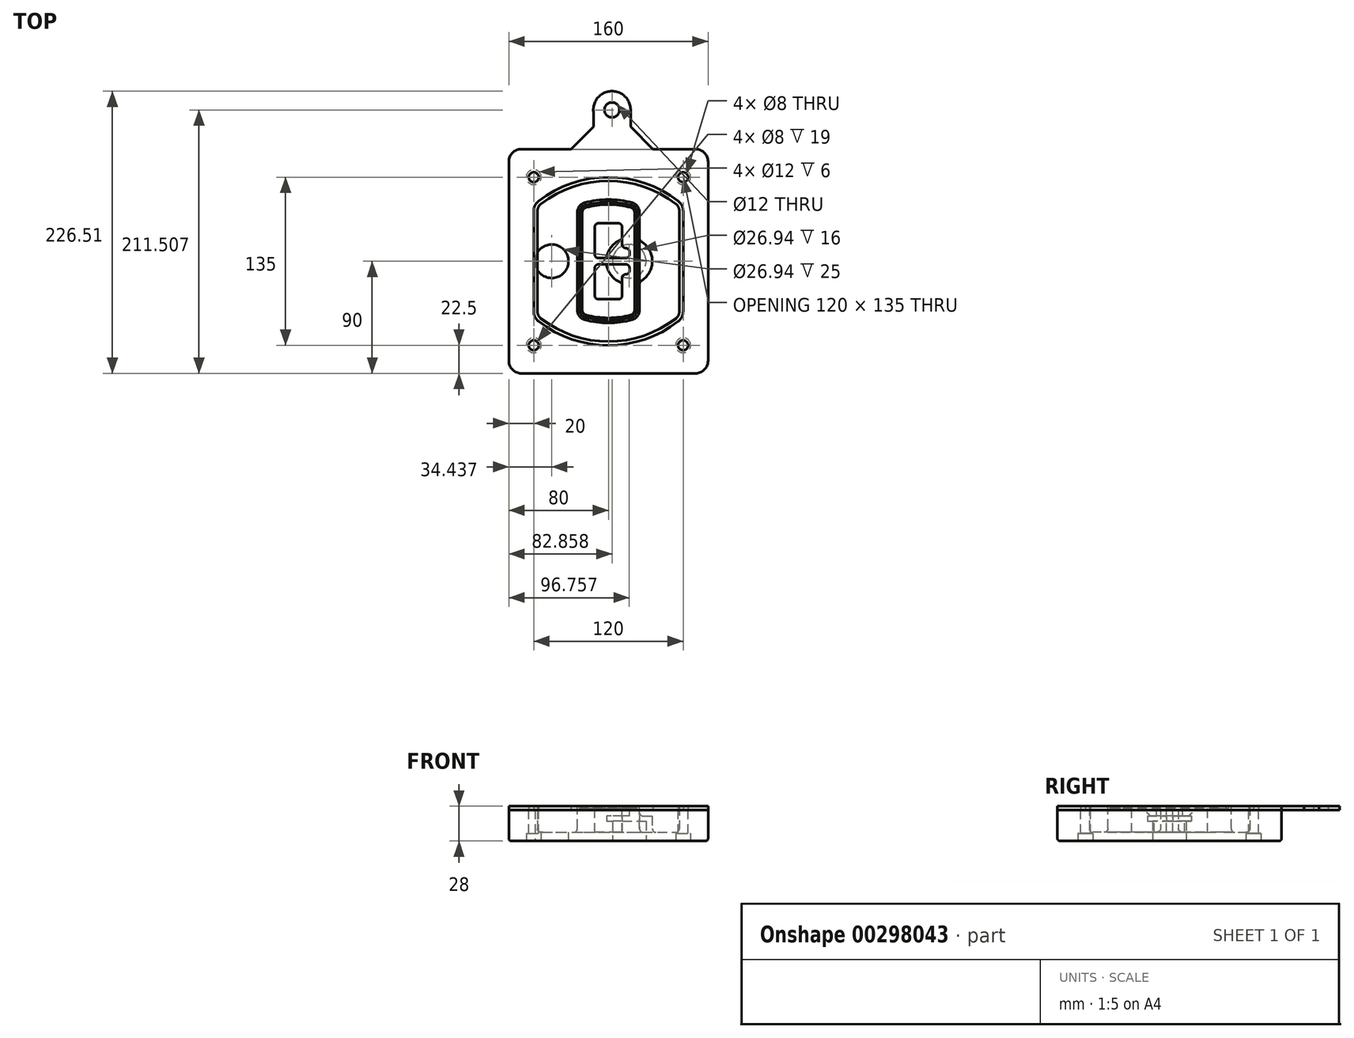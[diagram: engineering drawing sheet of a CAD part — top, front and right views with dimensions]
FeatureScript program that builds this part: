
annotation { "Feature Type Name" : "Feature", "Feature Type Description" : "" }
export const myFeature = defineFeature(function(context is Context, id is Id, definition is map)
    precondition{}
    {
        {
            var Q0;
            Q0=qCreatedBy(makeId("Top.planeOp"),FACE);
            var sketch = newSketch(context, id + "F0", { "sketchPlane" : qUnion([Q0])});
            skPoint(sketch, "E0.rect.middle", {"position": v(0, 0) * mm});
            skLineSegment(sketch, "E1.bottom", {"start": v(-70, -90) * mm, "end": v(70, -90) * mm});
            skLineSegment(sketch, "E1.top", {"start": v(-70, 90) * mm, "end": v(70, 90) * mm});
            skLineSegment(sketch, "E1.left", {"start": v(-80, -80) * mm, "end": v(-80, 80) * mm});
            skLineSegment(sketch, "E1.right", {"start": v(80, -80) * mm, "end": v(80, 80) * mm});
            skLineSegment(sketch, "E2", {"start": v(-80, 90) * mm, "end": v(80, -90) * mm, "construction": true});
            skLineSegment(sketch, "E3", {"start": v(80, 90) * mm, "end": v(-80, -90) * mm, "construction": true});
            skCircle(sketch, "E4", {"center": v(-60, 67.5) * mm, "radius": 4 * mm});
            skCircle(sketch, "E5", {"center": v(60, 67.5) * mm, "radius": 4 * mm});
            skCircle(sketch, "E6", {"center": v(60, -67.5) * mm, "radius": 4 * mm});
            skCircle(sketch, "E7", {"center": v(-60, -67.5) * mm, "radius": 4 * mm});
            skLineSegment(sketch, "E8", {"start": v(-60, 67.5) * mm, "end": v(60, 67.5) * mm, "construction": true});
            skLineSegment(sketch, "E9", {"start": v(60, 67.5) * mm, "end": v(60, -67.5) * mm, "construction": true});
            skLineSegment(sketch, "E10", {"start": v(60, -67.5) * mm, "end": v(-60, -67.5) * mm, "construction": true});
            skLineSegment(sketch, "E11", {"start": v(-60, -67.5) * mm, "end": v(-60, 67.5) * mm, "construction": true});
            skLineSegment(sketch, "E12", {"start": v(-60, 40.3) * mm, "end": v(-60, -40.3) * mm});
            skLineSegment(sketch, "E13", {"start": v(60, 40.3) * mm, "end": v(60, -40.3) * mm});
            skArc(sketch, "E14", {"start": v(56.15, 48.18) * mm, "mid": v(0, 67.5) * mm, "end": v(-56.15, 48.18) * mm});
            skArc(sketch, "E15", {"start": v(-56.15, -48.18) * mm, "mid": v(0, -67.5) * mm, "end": v(56.15, -48.18) * mm});
            skLineSegment(sketch, "E16", {"start": v(-60, 0) * mm, "end": v(60, 0) * mm, "construction": true});
            skPoint(sketch, "E17.visualSharp", {"position": v(-60, -45) * mm});
            skArc(sketch, "E17.filletArc", {"start": v(-60, -40.3) * mm, "mid": v(-58.99, -44.68) * mm, "end": v(-56.15, -48.18) * mm});
            skPoint(sketch, "E18.visualSharp", {"position": v(-60, 45) * mm});
            skArc(sketch, "E18.filletArc", {"start": v(-56.15, 48.18) * mm, "mid": v(-58.99, 44.68) * mm, "end": v(-60, 40.3) * mm});
            skPoint(sketch, "E19.visualSharp", {"position": v(60, 45) * mm});
            skArc(sketch, "E19.filletArc", {"start": v(60, 40.3) * mm, "mid": v(58.99, 44.68) * mm, "end": v(56.15, 48.18) * mm});
            skPoint(sketch, "E20.visualSharp", {"position": v(60, -45) * mm});
            skArc(sketch, "E20.filletArc", {"start": v(56.15, -48.18) * mm, "mid": v(58.99, -44.68) * mm, "end": v(60, -40.3) * mm});
            skPoint(sketch, "E21.visualSharp", {"position": v(-80, 90) * mm});
            skArc(sketch, "E21.filletArc", {"start": v(-70, 90) * mm, "mid": v(-77.07, 87.07) * mm, "end": v(-80, 80) * mm});
            skPoint(sketch, "E22.visualSharp", {"position": v(80, 90) * mm});
            skArc(sketch, "E22.filletArc", {"start": v(80, 80) * mm, "mid": v(77.07, 87.07) * mm, "end": v(70, 90) * mm});
            skPoint(sketch, "E23.visualSharp", {"position": v(80, -90) * mm});
            skArc(sketch, "E23.filletArc", {"start": v(70, -90) * mm, "mid": v(77.07, -87.07) * mm, "end": v(80, -80) * mm});
            skPoint(sketch, "E24.visualSharp", {"position": v(-80, -90) * mm});
            skArc(sketch, "E24.filletArc", {"start": v(-80, -80) * mm, "mid": v(-77.07, -87.07) * mm, "end": v(-70, -90) * mm});
            skArc(sketch, "E25.0", {"start": v(57, 40.3) * mm, "mid": v(56.3, 43.36) * mm, "end": v(54.3, 45.81) * mm});
            skLineSegment(sketch, "E25.1", {"start": v(57, 40.3) * mm, "end": v(57, -40.3) * mm});
            skArc(sketch, "E25.2", {"start": v(54.3, -45.81) * mm, "mid": v(56.3, -43.36) * mm, "end": v(57, -40.3) * mm});
            skArc(sketch, "E25.3", {"start": v(-54.3, -45.81) * mm, "mid": v(0, -64.5) * mm, "end": v(54.3, -45.81) * mm});
            skArc(sketch, "E25.4", {"start": v(-57, -40.3) * mm, "mid": v(-56.3, -43.36) * mm, "end": v(-54.3, -45.81) * mm});
            skArc(sketch, "E25.5", {"start": v(54.3, 45.81) * mm, "mid": v(0, 64.5) * mm, "end": v(-54.3, 45.81) * mm});
            skLineSegment(sketch, "E25.6", {"start": v(-57, 40.3) * mm, "end": v(-57, -40.3) * mm});
            skArc(sketch, "E25.7", {"start": v(-54.3, 45.81) * mm, "mid": v(-56.3, 43.36) * mm, "end": v(-57, 40.3) * mm});
            skArc(sketch, "E26.0", {"start": v(-58.62, 51.33) * mm, "mid": v(-62.58, 46.43) * mm, "end": v(-64, 40.3) * mm});
            skArc(sketch, "E26.1", {"start": v(58.62, 51.33) * mm, "mid": v(0, 71.5) * mm, "end": v(-58.62, 51.33) * mm});
            skArc(sketch, "E26.2", {"start": v(64, 40.3) * mm, "mid": v(62.58, 46.43) * mm, "end": v(58.62, 51.33) * mm});
            skLineSegment(sketch, "E26.3", {"start": v(64, 40.3) * mm, "end": v(64, -40.3) * mm});
            skArc(sketch, "E26.4", {"start": v(58.62, -51.33) * mm, "mid": v(62.58, -46.43) * mm, "end": v(64, -40.3) * mm});
            skLineSegment(sketch, "E26.5", {"start": v(-64, 40.3) * mm, "end": v(-64, -40.3) * mm});
            skArc(sketch, "E26.6", {"start": v(-58.62, -51.33) * mm, "mid": v(0, -71.5) * mm, "end": v(58.62, -51.33) * mm});
            skArc(sketch, "E26.7", {"start": v(-64, -40.3) * mm, "mid": v(-62.58, -46.43) * mm, "end": v(-58.62, -51.33) * mm});
            skSolve(sketch);
        }
        {
            var Q0;
            Q0=makeQuery(id+"F0.imprint","IMPRINT",FACE,{"disambiguationData":[TD([[makeQuery(id+"F0.imprint","IMPRINT",EDGE,{"derivedFrom":sQuery(id+"F0.wireOp",EDGE,"E1.bottom")}),1.0]])]});
            var Q1;
            Q1=makeQuery(id+"F0.imprint","IMPRINT",FACE,{"disambiguationData":[TD([[makeQuery(id+"F0.imprint","IMPRINT",EDGE,{"derivedFrom":sQuery(id+"F0.wireOp",EDGE,"E12")}),1.0]])]});
            var Q2;
            Q2=makeQuery(id+"F0.imprint","IMPRINT",FACE,{"disambiguationData":[TD([[makeQuery(id+"F0.imprint","IMPRINT",EDGE,{"derivedFrom":sQuery(id+"F0.wireOp",EDGE,"E25.0")}),1.0]])]});
            var Q3;
            Q3=makeQuery(id+"F0.imprint","IMPRINT",FACE,{"disambiguationData":[TD([[makeQuery(id+"F0.imprint","IMPRINT",EDGE,{"derivedFrom":sQuery(id+"F0.wireOp",EDGE,"E12")}),-1.0]])]});
            extrude(context, id + "F1", {"entities" : qUnion([Q0, Q1, Q2, Q3]), "oppositeDirection" : true, "depth" : 25 * mm});
        }
        {
            var Q0;
            Q0=makeQuery(id+"F0.imprint","IMPRINT",FACE,{"disambiguationData":[TD([[makeQuery(id+"F0.imprint","IMPRINT",EDGE,{"derivedFrom":sQuery(id+"F0.wireOp",EDGE,"E12")}),1.0]])]});
            extrude(context, id + "F2", {"entities" : qUnion([Q0]), "operationType" : NewBodyOperationType.ADD, "depth" : 3 * mm});
        }
        {
            var Q0;
            Q0=makeQuery(id+"F0.imprint","IMPRINT",FACE,{"disambiguationData":[TD([[makeQuery(id+"F0.imprint","IMPRINT",EDGE,{"derivedFrom":sQuery(id+"F0.wireOp",EDGE,"E25.0")}),1.0]])]});
            extrude(context, id + "F3", {"entities" : qUnion([Q0]), "operationType" : NewBodyOperationType.REMOVE, "oppositeDirection" : true, "depth" : 18 * mm});
        }
        {
            var Q0;
            Q0=makeQuery(id+"F2.opExtrude","CAP_FACE",FACE,{"disambiguationData":[OSD([sQuery(id+"F0.wireOp",EDGE,"E12"),sQuery(id+"F0.wireOp",EDGE,"E13"),sQuery(id+"F0.wireOp",EDGE,"E14"),sQuery(id+"F0.wireOp",EDGE,"E15"),sQuery(id+"F0.wireOp",EDGE,"E17.filletArc"),sQuery(id+"F0.wireOp",EDGE,"E18.filletArc"),sQuery(id+"F0.wireOp",EDGE,"E19.filletArc"),sQuery(id+"F0.wireOp",EDGE,"E20.filletArc"),sQuery(id+"F0.wireOp",EDGE,"E25.0"),sQuery(id+"F0.wireOp",EDGE,"E25.1"),sQuery(id+"F0.wireOp",EDGE,"E25.2"),sQuery(id+"F0.wireOp",EDGE,"E25.3"),sQuery(id+"F0.wireOp",EDGE,"E25.4"),sQuery(id+"F0.wireOp",EDGE,"E25.5"),sQuery(id+"F0.wireOp",EDGE,"E25.6"),sQuery(id+"F0.wireOp",EDGE,"E25.7")])],"isStart":false});
            var sketch = newSketch(context, id + "F4", { "sketchPlane" : qUnion([Q0])});
            skArc(sketch, "E27.0", {"start": v(-19.08, -46.97) * mm, "mid": v(0, -49.5) * mm, "end": v(19.08, -46.97) * mm});
            skArc(sketch, "E28.0", {"start": v(19.08, 46.97) * mm, "mid": v(0, 49.5) * mm, "end": v(-19.08, 46.97) * mm});
            skLineSegment(sketch, "E29", {"start": v(-25, 39.25) * mm, "end": v(-25, -39.25) * mm});
            skLineSegment(sketch, "E30", {"start": v(25, 39.25) * mm, "end": v(25, -39.25) * mm});
            skLineSegment(sketch, "E31", {"start": v(-25, 45.1) * mm, "end": v(25, 45.1) * mm, "construction": true});
            skLineSegment(sketch, "E32", {"start": v(-25, -45.1) * mm, "end": v(25, -45.1) * mm, "construction": true});
            skPoint(sketch, "E33.visualSharp", {"position": v(-25, 45.1) * mm});
            skArc(sketch, "E33.filletArc", {"start": v(-19.08, 46.97) * mm, "mid": v(-23.35, 44.11) * mm, "end": v(-25, 39.25) * mm});
            skPoint(sketch, "E34.visualSharp", {"position": v(25, 45.1) * mm});
            skArc(sketch, "E34.filletArc", {"start": v(25, 39.25) * mm, "mid": v(23.35, 44.11) * mm, "end": v(19.08, 46.97) * mm});
            skPoint(sketch, "E35.visualSharp", {"position": v(25, -45.1) * mm});
            skArc(sketch, "E35.filletArc", {"start": v(19.08, -46.97) * mm, "mid": v(23.35, -44.11) * mm, "end": v(25, -39.25) * mm});
            skPoint(sketch, "E36.visualSharp", {"position": v(-25, -45.1) * mm});
            skArc(sketch, "E36.filletArc", {"start": v(-25, -39.25) * mm, "mid": v(-23.35, -44.11) * mm, "end": v(-19.08, -46.97) * mm});
            skArc(sketch, "E37.0", {"start": v(54.3, 45.81) * mm, "mid": v(0, 64.5) * mm, "end": v(-54.3, 45.81) * mm});
            skArc(sketch, "E37.1", {"start": v(-54.3, 45.81) * mm, "mid": v(-56.3, 43.36) * mm, "end": v(-57, 40.3) * mm});
            skLineSegment(sketch, "E37.2", {"start": v(-57, 40.3) * mm, "end": v(-57, -40.3) * mm});
            skArc(sketch, "E37.3", {"start": v(-57, -40.3) * mm, "mid": v(-56.3, -43.36) * mm, "end": v(-54.3, -45.81) * mm});
            skArc(sketch, "E37.4", {"start": v(-54.3, -45.81) * mm, "mid": v(0, -64.5) * mm, "end": v(54.3, -45.81) * mm});
            skArc(sketch, "E37.5", {"start": v(54.3, -45.81) * mm, "mid": v(56.3, -43.36) * mm, "end": v(57, -40.3) * mm});
            skLineSegment(sketch, "E37.6", {"start": v(57, 40.3) * mm, "end": v(57, -40.3) * mm});
            skArc(sketch, "E37.7", {"start": v(57, 40.3) * mm, "mid": v(56.3, 43.36) * mm, "end": v(54.3, 45.81) * mm});
            skLineSegment(sketch, "E38.0", {"start": v(23, 39.25) * mm, "end": v(23, -39.25) * mm});
            skArc(sketch, "E38.1", {"start": v(18.56, -45.04) * mm, "mid": v(21.76, -42.9) * mm, "end": v(23, -39.25) * mm});
            skArc(sketch, "E38.2", {"start": v(-18.56, -45.04) * mm, "mid": v(0, -47.5) * mm, "end": v(18.56, -45.04) * mm});
            skArc(sketch, "E38.3", {"start": v(-23, -39.25) * mm, "mid": v(-21.76, -42.9) * mm, "end": v(-18.56, -45.04) * mm});
            skLineSegment(sketch, "E38.4", {"start": v(-23, 39.25) * mm, "end": v(-23, -39.25) * mm});
            skArc(sketch, "E38.5", {"start": v(23, 39.25) * mm, "mid": v(21.76, 42.9) * mm, "end": v(18.56, 45.04) * mm});
            skArc(sketch, "E38.6", {"start": v(-18.56, 45.04) * mm, "mid": v(-21.76, 42.9) * mm, "end": v(-23, 39.25) * mm});
            skArc(sketch, "E38.7", {"start": v(18.56, 45.04) * mm, "mid": v(0, 47.5) * mm, "end": v(-18.56, 45.04) * mm});
            skArc(sketch, "E39.0", {"start": v(21, 39.25) * mm, "mid": v(20.18, 41.68) * mm, "end": v(18.04, 43.1) * mm});
            skLineSegment(sketch, "E39.1", {"start": v(21, 39.25) * mm, "end": v(21, -39.25) * mm});
            skArc(sketch, "E39.2", {"start": v(18.04, -43.1) * mm, "mid": v(20.18, -41.68) * mm, "end": v(21, -39.25) * mm});
            skArc(sketch, "E39.3", {"start": v(-18.04, -43.1) * mm, "mid": v(0, -45.5) * mm, "end": v(18.04, -43.1) * mm});
            skArc(sketch, "E39.4", {"start": v(-21, -39.25) * mm, "mid": v(-20.18, -41.68) * mm, "end": v(-18.04, -43.1) * mm});
            skArc(sketch, "E39.5", {"start": v(18.04, 43.1) * mm, "mid": v(0, 45.5) * mm, "end": v(-18.04, 43.1) * mm});
            skLineSegment(sketch, "E39.6", {"start": v(-21, 39.25) * mm, "end": v(-21, -39.25) * mm});
            skArc(sketch, "E39.7", {"start": v(-18.04, 43.1) * mm, "mid": v(-20.18, 41.68) * mm, "end": v(-21, 39.25) * mm});
            skLineSegment(sketch, "E40", {"start": v(-25, 0) * mm, "end": v(25, 0) * mm, "construction": true});
            skLineSegment(sketch, "E41", {"start": v(-11, 5.5) * mm, "end": v(-11, 27.5) * mm});
            skLineSegment(sketch, "E42", {"start": v(-8, 30.5) * mm, "end": v(8, 30.5) * mm});
            skLineSegment(sketch, "E43", {"start": v(11, 27.5) * mm, "end": v(11, 13.5) * mm});
            skLineSegment(sketch, "E44", {"start": v(14, 10.5) * mm, "end": v(14, 10.5) * mm});
            skLineSegment(sketch, "E45", {"start": v(17, 7.5) * mm, "end": v(17, 5.5) * mm});
            skLineSegment(sketch, "E46", {"start": v(14, 2.5) * mm, "end": v(-8, 2.5) * mm});
            skPoint(sketch, "E47.visualSharp", {"position": v(-11, 30.5) * mm});
            skArc(sketch, "E47.filletArc", {"start": v(-8, 30.5) * mm, "mid": v(-10.12, 29.62) * mm, "end": v(-11, 27.5) * mm});
            skPoint(sketch, "E48.visualSharp", {"position": v(11, 30.5) * mm});
            skArc(sketch, "E48.filletArc", {"start": v(11, 27.5) * mm, "mid": v(10.12, 29.62) * mm, "end": v(8, 30.5) * mm});
            skPoint(sketch, "E49.visualSharp", {"position": v(11, 10.5) * mm});
            skArc(sketch, "E49.filletArc", {"start": v(11, 13.5) * mm, "mid": v(11.88, 11.38) * mm, "end": v(14, 10.5) * mm});
            skPoint(sketch, "E50.visualSharp", {"position": v(17, 10.5) * mm});
            skArc(sketch, "E50.filletArc", {"start": v(17, 7.5) * mm, "mid": v(16.12, 9.62) * mm, "end": v(14, 10.5) * mm});
            skPoint(sketch, "E51.visualSharp", {"position": v(17, 2.5) * mm});
            skArc(sketch, "E51.filletArc", {"start": v(14, 2.5) * mm, "mid": v(16.12, 3.38) * mm, "end": v(17, 5.5) * mm});
            skPoint(sketch, "E52.visualSharp", {"position": v(-11, 2.5) * mm});
            skArc(sketch, "E52.filletArc", {"start": v(-11, 5.5) * mm, "mid": v(-10.12, 3.38) * mm, "end": v(-8, 2.5) * mm});
            skLineSegment(sketch, "E53.0.MirrorCS", {"start": v(14, -2.5) * mm, "end": v(-8, -2.5) * mm});
            skArc(sketch, "E54.0.MirrorCS", {"start": v(-11, -5.5) * mm, "mid": v(-10.12, -3.38) * mm, "end": v(-8, -2.5) * mm});
            skLineSegment(sketch, "E55.0.MirrorCS", {"start": v(-11, -5.5) * mm, "end": v(-11, -27.5) * mm});
            skArc(sketch, "E56.0.MirrorCS", {"start": v(-8, -30.5) * mm, "mid": v(-10.12, -29.62) * mm, "end": v(-11, -27.5) * mm});
            skLineSegment(sketch, "E57.0.MirrorCS", {"start": v(-8, -30.5) * mm, "end": v(8, -30.5) * mm});
            skArc(sketch, "E58.0.MirrorCS", {"start": v(11, -27.5) * mm, "mid": v(10.12, -29.62) * mm, "end": v(8, -30.5) * mm});
            skLineSegment(sketch, "E59.0.MirrorCS", {"start": v(11, -27.5) * mm, "end": v(11, -13.5) * mm});
            skArc(sketch, "E60.0.MirrorCS", {"start": v(11, -13.5) * mm, "mid": v(11.88, -11.38) * mm, "end": v(14, -10.5) * mm});
            skArc(sketch, "E61.0.MirrorCS", {"start": v(17, -7.5) * mm, "mid": v(16.12, -9.62) * mm, "end": v(14, -10.5) * mm});
            skLineSegment(sketch, "E62.0.MirrorCS", {"start": v(17, -7.5) * mm, "end": v(17, -5.5) * mm});
            skArc(sketch, "E63.0.MirrorCS", {"start": v(14, -2.5) * mm, "mid": v(16.12, -3.38) * mm, "end": v(17, -5.5) * mm});
            skSolve(sketch);
        }
        {
            var Q0;
            Q0=makeQuery(id+"F4.imprint","IMPRINT",FACE,{"disambiguationData":[TD([[makeQuery(id+"F4.imprint","IMPRINT",EDGE,{"derivedFrom":sQuery(id+"F4.wireOp",EDGE,"E27.0")}),1.0]])]});
            var Q1;
            Q1=makeQuery(id+"F4.imprint","IMPRINT",FACE,{"disambiguationData":[TD([[makeQuery(id+"F4.imprint","IMPRINT",EDGE,{"derivedFrom":sQuery(id+"F4.wireOp",EDGE,"E38.0")}),-1.0]])]});
            var Q2;
            Q2=makeQuery(id+"F4.imprint","IMPRINT",FACE,{"disambiguationData":[TD([[makeQuery(id+"F4.imprint","IMPRINT",EDGE,{"derivedFrom":sQuery(id+"F4.wireOp",EDGE,"E39.0")}),1.0]])]});
            extrude(context, id + "F5", {"entities" : qUnion([Q0, Q1, Q2]), "operationType" : NewBodyOperationType.ADD, "endBound" : BoundingType.UP_TO_NEXT, "oppositeDirection" : true, "depth" : 25 * mm});
        }
        {
            var Q0;
            Q0=makeQuery(id+"F4.imprint","IMPRINT",FACE,{"disambiguationData":[TD([[makeQuery(id+"F4.imprint","IMPRINT",EDGE,{"derivedFrom":sQuery(id+"F4.wireOp",EDGE,"E38.0")}),-1.0]])]});
            extrude(context, id + "F6", {"entities" : qUnion([Q0]), "operationType" : NewBodyOperationType.REMOVE, "oppositeDirection" : true, "depth" : 2 * mm});
        }
        {
            var Q0;
            Q0=makeQuery(id+"F1.opExtrude","CAP_FACE",FACE,{"disambiguationData":[OSD([sQuery(id+"F0.wireOp",EDGE,"E1.bottom"),sQuery(id+"F0.wireOp",EDGE,"E1.top"),sQuery(id+"F0.wireOp",EDGE,"E1.left"),sQuery(id+"F0.wireOp",EDGE,"E1.right"),sQuery(id+"F0.wireOp",EDGE,"E4"),sQuery(id+"F0.wireOp",EDGE,"E5"),sQuery(id+"F0.wireOp",EDGE,"E6"),sQuery(id+"F0.wireOp",EDGE,"E7"),sQuery(id+"F0.wireOp",EDGE,"E21.filletArc"),sQuery(id+"F0.wireOp",EDGE,"E22.filletArc"),sQuery(id+"F0.wireOp",EDGE,"E23.filletArc"),sQuery(id+"F0.wireOp",EDGE,"E24.filletArc")])],"isStart":false});
            var sketch = newSketch(context, id + "F7", { "sketchPlane" : qUnion([Q0])});
            skCircle(sketch, "E64", {"center": v(16.76, 0) * mm, "radius": 13.47 * mm});
            skCircle(sketch, "E65", {"center": v(-45.56, 0) * mm, "radius": 13.47 * mm});
            skLineSegment(sketch, "E66", {"start": v(80, 0) * mm, "end": v(-80, 0) * mm});
            skCircle(sketch, "E67", {"center": v(16.76, 0) * mm, "radius": 18.47 * mm});
            skCircle(sketch, "E68", {"center": v(60, -67.5) * mm, "radius": 6 * mm});
            skCircle(sketch, "E69", {"center": v(-60, -67.5) * mm, "radius": 6 * mm});
            skCircle(sketch, "E70", {"center": v(-60, 67.5) * mm, "radius": 6 * mm});
            skCircle(sketch, "E71", {"center": v(60, 67.5) * mm, "radius": 6 * mm});
            skSolve(sketch);
        }
        {
            var Q0;
            {var subQ1=sQuery(id+"F7.wireOp",EDGE,"E66");var subQ4=sQuery(id+"F7.wireOp",EDGE,"E64");var subQ6=makeQuery(id+"F7.imprint","INTERSECT",VERTEX,{"disambiguationData":[OD(0.0)],"derivedFrom":[subQ4,subQ1]});Q0=makeQuery(id+"F7.imprint","IMPRINT",FACE,{"disambiguationData":[TD([[makeQuery(id+"F7.imprint","IMPRINT",EDGE,{"disambiguationData":[TD([[subQ6,-1.0]])],"derivedFrom":subQ4}),-1.0]])]});}
            var Q1;
            {var subQ0=sQuery(id+"F7.wireOp",EDGE,"E66");var subQ1=sQuery(id+"F7.wireOp",EDGE,"E64");var subQ3=makeQuery(id+"F7.imprint","INTERSECT",VERTEX,{"disambiguationData":[OD(0.0)],"derivedFrom":[subQ1,subQ0]});Q1=makeQuery(id+"F7.imprint","IMPRINT",FACE,{"disambiguationData":[TD([[makeQuery(id+"F7.imprint","IMPRINT",EDGE,{"disambiguationData":[TD([[subQ3,-1.0]])],"derivedFrom":subQ1}),1.0]])]});}
            var Q2;
            {var subQ0=sQuery(id+"F7.wireOp",EDGE,"E66");var subQ1=sQuery(id+"F7.wireOp",EDGE,"E64");var subQ3=makeQuery(id+"F7.imprint","INTERSECT",VERTEX,{"disambiguationData":[OD(0.0)],"derivedFrom":[subQ1,subQ0]});Q2=makeQuery(id+"F7.imprint","IMPRINT",FACE,{"disambiguationData":[TD([[makeQuery(id+"F7.imprint","IMPRINT",EDGE,{"disambiguationData":[TD([[subQ3,1.0]])],"derivedFrom":subQ1}),1.0]])]});}
            var Q3;
            {var subQ1=sQuery(id+"F7.wireOp",EDGE,"E66");var subQ4=sQuery(id+"F7.wireOp",EDGE,"E64");var subQ6=makeQuery(id+"F7.imprint","INTERSECT",VERTEX,{"disambiguationData":[OD(0.0)],"derivedFrom":[subQ4,subQ1]});Q3=makeQuery(id+"F7.imprint","IMPRINT",FACE,{"disambiguationData":[TD([[makeQuery(id+"F7.imprint","IMPRINT",EDGE,{"disambiguationData":[TD([[subQ6,1.0]])],"derivedFrom":subQ4}),-1.0]])]});}
            extrude(context, id + "F8", {"entities" : qUnion([Q0, Q1, Q2, Q3]), "operationType" : NewBodyOperationType.ADD, "oppositeDirection" : true, "depth" : 20 * mm});
        }
        {
            var Q0;
            {var subQ0=sQuery(id+"F7.wireOp",EDGE,"E66");var subQ1=sQuery(id+"F7.wireOp",EDGE,"E64");var subQ3=makeQuery(id+"F7.imprint","INTERSECT",VERTEX,{"disambiguationData":[OD(0.0)],"derivedFrom":[subQ1,subQ0]});Q0=makeQuery(id+"F7.imprint","IMPRINT",FACE,{"disambiguationData":[TD([[makeQuery(id+"F7.imprint","IMPRINT",EDGE,{"disambiguationData":[TD([[subQ3,-1.0]])],"derivedFrom":subQ1}),1.0]])]});}
            var Q1;
            {var subQ0=sQuery(id+"F7.wireOp",EDGE,"E66");var subQ1=sQuery(id+"F7.wireOp",EDGE,"E64");var subQ3=makeQuery(id+"F7.imprint","INTERSECT",VERTEX,{"disambiguationData":[OD(0.0)],"derivedFrom":[subQ1,subQ0]});Q1=makeQuery(id+"F7.imprint","IMPRINT",FACE,{"disambiguationData":[TD([[makeQuery(id+"F7.imprint","IMPRINT",EDGE,{"disambiguationData":[TD([[subQ3,1.0]])],"derivedFrom":subQ1}),1.0]])]});}
            extrude(context, id + "F9", {"entities" : qUnion([Q0, Q1]), "operationType" : NewBodyOperationType.REMOVE, "oppositeDirection" : true, "depth" : 16 * mm});
        }
        {
            var Q0;
            {var subQ0=sQuery(id+"F7.wireOp",EDGE,"E66");var subQ1=sQuery(id+"F7.wireOp",EDGE,"E65");var subQ3=makeQuery(id+"F7.imprint","INTERSECT",VERTEX,{"disambiguationData":[OD(0.0)],"derivedFrom":[subQ1,subQ0]});Q0=makeQuery(id+"F7.imprint","IMPRINT",FACE,{"disambiguationData":[TD([[makeQuery(id+"F7.imprint","IMPRINT",EDGE,{"disambiguationData":[TD([[subQ3,-1.0]])],"derivedFrom":subQ1}),1.0]])]});}
            var Q1;
            {var subQ0=sQuery(id+"F7.wireOp",EDGE,"E66");var subQ1=sQuery(id+"F7.wireOp",EDGE,"E65");var subQ3=makeQuery(id+"F7.imprint","INTERSECT",VERTEX,{"disambiguationData":[OD(0.0)],"derivedFrom":[subQ1,subQ0]});Q1=makeQuery(id+"F7.imprint","IMPRINT",FACE,{"disambiguationData":[TD([[makeQuery(id+"F7.imprint","IMPRINT",EDGE,{"disambiguationData":[TD([[subQ3,1.0]])],"derivedFrom":subQ1}),1.0]])]});}
            extrude(context, id + "F10", {"entities" : qUnion([Q0, Q1]), "operationType" : NewBodyOperationType.REMOVE, "oppositeDirection" : true, "depth" : 25 * mm});
        }
        {
            var Q0;
            Q0=makeQuery(id+"F7.imprint","IMPRINT",FACE,{"disambiguationData":[TD([[makeQuery(id+"F7.imprint","IMPRINT",EDGE,{"derivedFrom":sQuery(id+"F7.wireOp",EDGE,"E68")}),1.0]])]});
            var Q1;
            Q1=makeQuery(id+"F7.imprint","IMPRINT",FACE,{"disambiguationData":[TD([[makeQuery(id+"F7.imprint","IMPRINT",EDGE,{"derivedFrom":makeQuery(id+"F1.opExtrude","CAP_EDGE",EDGE,{"disambiguationData":[OSD([sQuery(id+"F0.wireOp",EDGE,"E5")])],"isStart":false})}),-1.0]])]});
            var Q2;
            Q2=makeQuery(id+"F7.imprint","IMPRINT",FACE,{"disambiguationData":[TD([[makeQuery(id+"F7.imprint","IMPRINT",EDGE,{"derivedFrom":sQuery(id+"F7.wireOp",EDGE,"E69")}),1.0]])]});
            var Q3;
            Q3=makeQuery(id+"F7.imprint","IMPRINT",FACE,{"disambiguationData":[TD([[makeQuery(id+"F7.imprint","IMPRINT",EDGE,{"derivedFrom":makeQuery(id+"F1.opExtrude","CAP_EDGE",EDGE,{"disambiguationData":[OSD([sQuery(id+"F0.wireOp",EDGE,"E4")])],"isStart":false})}),-1.0]])]});
            var Q4;
            Q4=makeQuery(id+"F7.imprint","IMPRINT",FACE,{"disambiguationData":[TD([[makeQuery(id+"F7.imprint","IMPRINT",EDGE,{"derivedFrom":sQuery(id+"F7.wireOp",EDGE,"E70")}),1.0]])]});
            var Q5;
            Q5=makeQuery(id+"F7.imprint","IMPRINT",FACE,{"disambiguationData":[TD([[makeQuery(id+"F7.imprint","IMPRINT",EDGE,{"derivedFrom":makeQuery(id+"F1.opExtrude","CAP_EDGE",EDGE,{"disambiguationData":[OSD([sQuery(id+"F0.wireOp",EDGE,"E7")])],"isStart":false})}),-1.0]])]});
            var Q6;
            Q6=makeQuery(id+"F7.imprint","IMPRINT",FACE,{"disambiguationData":[TD([[makeQuery(id+"F7.imprint","IMPRINT",EDGE,{"derivedFrom":sQuery(id+"F7.wireOp",EDGE,"E71")}),1.0]])]});
            var Q7;
            Q7=makeQuery(id+"F7.imprint","IMPRINT",FACE,{"disambiguationData":[TD([[makeQuery(id+"F7.imprint","IMPRINT",EDGE,{"derivedFrom":makeQuery(id+"F1.opExtrude","CAP_EDGE",EDGE,{"disambiguationData":[OSD([sQuery(id+"F0.wireOp",EDGE,"E6")])],"isStart":false})}),-1.0]])]});
            extrude(context, id + "F11", {"entities" : qUnion([Q0, Q1, Q2, Q3, Q4, Q5, Q6, Q7]), "operationType" : NewBodyOperationType.REMOVE, "oppositeDirection" : true, "depth" : 6 * mm});
        }
        {
            var Q0;
            Q0=makeQuery(id+"F9.boolean.opBoolean","COPY",FACE,{"derivedFrom":makeQuery(id+"F9.opExtrude","CAP_FACE",FACE,{"disambiguationData":[OSD([sQuery(id+"F7.wireOp",EDGE,"E64")])],"isStart":false})});
            var sketch = newSketch(context, id + "F12", { "sketchPlane" : qUnion([Q0])});
            skArc(sketch, "E72.0", {"start": v(11, 17.55) * mm, "mid": v(2.57, 11.82) * mm, "end": v(-1.54, 2.5) * mm});
            skArc(sketch, "E72.1", {"start": v(-1.54, -2.5) * mm, "mid": v(2.57, -11.82) * mm, "end": v(11, -17.55) * mm});
            skLineSegment(sketch, "E73", {"start": v(-1.54, -2.5) * mm, "end": v(14, -2.5) * mm});
            skLineSegment(sketch, "E74.0", {"start": v(14, 2.5) * mm, "end": v(-1.54, 2.5) * mm});
            skArc(sketch, "E74.1", {"start": v(14, 2.5) * mm, "mid": v(16.12, 3.38) * mm, "end": v(17, 5.5) * mm});
            skLineSegment(sketch, "E74.2", {"start": v(17, 7.5) * mm, "end": v(17, 5.5) * mm});
            skArc(sketch, "E74.3", {"start": v(17, 7.5) * mm, "mid": v(16.12, 9.62) * mm, "end": v(14, 10.5) * mm});
            skArc(sketch, "E74.4", {"start": v(11, 13.5) * mm, "mid": v(11.88, 11.38) * mm, "end": v(14, 10.5) * mm});
            skLineSegment(sketch, "E74.5", {"start": v(11, 17.55) * mm, "end": v(11, 13.5) * mm});
            skLineSegment(sketch, "E74.7", {"start": v(14, -2.5) * mm, "end": v(-1.54, -2.5) * mm});
            skArc(sketch, "E74.8", {"start": v(14, -2.5) * mm, "mid": v(16.12, -3.38) * mm, "end": v(17, -5.5) * mm});
            skLineSegment(sketch, "E74.9", {"start": v(17, -7.5) * mm, "end": v(17, -5.5) * mm});
            skArc(sketch, "E74.10", {"start": v(17, -7.5) * mm, "mid": v(16.12, -9.62) * mm, "end": v(14, -10.5) * mm});
            skArc(sketch, "E74.11", {"start": v(11, -13.5) * mm, "mid": v(11.88, -11.38) * mm, "end": v(14, -10.5) * mm});
            skLineSegment(sketch, "E74.12", {"start": v(11, -17.55) * mm, "end": v(11, -13.5) * mm});
            skPoint(sketch, "E75.orphan", {"position": v(11, -27.5) * mm});
            skPoint(sketch, "E76.orphan", {"position": v(-8, -2.5) * mm});
            skPoint(sketch, "E77.orphan", {"position": v(-8, 2.5) * mm});
            skPoint(sketch, "E78.orphan", {"position": v(11, 27.5) * mm});
            skSolve(sketch);
        }
        {
            var Q0;
            {var subQ7=sQuery(id+"F12.wireOp",EDGE,"E72.0");var subQ14=sQuery(id+"F12.wireOp",EDGE,"E72.1");var subQ16=sQuery(id+"F12.wireOp",EDGE,"E74.1");var subQ18=sQuery(id+"F12.wireOp",EDGE,"E74.8");Q0=qUnion([makeQuery(id+"F12.imprint","IMPRINT",FACE,{"disambiguationData":[TD([[makeQuery(id+"F12.imprint","IMPRINT",EDGE,{"derivedFrom":subQ7}),1.0]])]}),makeQuery(id+"F12.imprint","IMPRINT",FACE,{"disambiguationData":[TD([[makeQuery(id+"F12.imprint","IMPRINT",EDGE,{"derivedFrom":subQ14}),1.0]])]}),makeQuery(id+"F12.imprint","IMPRINT",FACE,{"disambiguationData":[TD([[makeQuery(id+"F12.imprint","IMPRINT",EDGE,{"derivedFrom":subQ16}),1.0]])]}),makeQuery(id+"F12.imprint","IMPRINT",FACE,{"disambiguationData":[TD([[makeQuery(id+"F12.imprint","IMPRINT",EDGE,{"derivedFrom":subQ18}),-1.0]])]})]);}
            var Q1;
            Q1=makeQuery(id+"F5.boolean.opBoolean","SPLIT",FACE,{"disambiguationData":[TD([makeQuery(id+"F5.opExtrude","SWEPT_FACE",FACE,{"disambiguationData":[OSD([sQuery(id+"F4.wireOp",EDGE,"E41")])]})])],"derivedFrom":makeQuery(id+"F3.boolean.opBoolean","COPY",FACE,{"derivedFrom":makeQuery(id+"F3.opExtrude","CAP_FACE",FACE,{"disambiguationData":[OSD([sQuery(id+"F0.wireOp",EDGE,"E25.0"),sQuery(id+"F0.wireOp",EDGE,"E25.1"),sQuery(id+"F0.wireOp",EDGE,"E25.2"),sQuery(id+"F0.wireOp",EDGE,"E25.3"),sQuery(id+"F0.wireOp",EDGE,"E25.4"),sQuery(id+"F0.wireOp",EDGE,"E25.5"),sQuery(id+"F0.wireOp",EDGE,"E25.6"),sQuery(id+"F0.wireOp",EDGE,"E25.7")])],"isStart":false})})});
            extrude(context, id + "F13", {"entities" : qUnion([Q0]), "operationType" : NewBodyOperationType.REMOVE, "endBound" : BoundingType.UP_TO_SURFACE, "endBoundEntityFace" : qUnion([Q1]), "depth" : 25 * mm});
        }
        {
            var Q0;
            Q0=makeQuery(id+"F3.boolean.opBoolean","COPY",EDGE,{"derivedFrom":makeQuery(id+"F3.opExtrude","CAP_EDGE",EDGE,{"disambiguationData":[OSD([sQuery(id+"F0.wireOp",EDGE,"E25.6")])],"isStart":false})});
            var Q1;
            Q1=makeQuery(id+"F8.boolean.opBoolean","INTERSECT",EDGE,{"derivedFrom":[makeQuery(id+"F5.opExtrude","SWEPT_FACE",FACE,{"disambiguationData":[OSD([sQuery(id+"F4.wireOp",EDGE,"E30")])]}),makeQuery(id+"F8.opExtrude","CAP_FACE",FACE,{"disambiguationData":[OSD([sQuery(id+"F7.wireOp",EDGE,"E67")])],"isStart":false})]});
            var Q2;
            Q2=makeQuery(id+"F8.boolean.opBoolean","INTERSECT",EDGE,{"disambiguationData":[OD(1.0)],"derivedFrom":[makeQuery(id+"F5.opExtrude","SWEPT_FACE",FACE,{"disambiguationData":[OSD([sQuery(id+"F4.wireOp",EDGE,"E30")])]}),makeQuery(id+"F8.opExtrude","SWEPT_FACE",FACE,{"disambiguationData":[OSD([sQuery(id+"F7.wireOp",EDGE,"E67")])]})]});
            var Q3;
            {var subQ0=sQuery(id+"F4.wireOp",EDGE,"E30");Q3=makeQuery(id+"F8.boolean.opBoolean","SPLIT",EDGE,{"disambiguationData":[TD([makeQuery(id+"F5.opExtrude","SWEPT_FACE",FACE,{"disambiguationData":[OSD([sQuery(id+"F4.wireOp",EDGE,"E35.filletArc")])]})])],"derivedFrom":makeQuery(id+"F5.opExtrude","CAP_EDGE",EDGE,{"disambiguationData":[OSD([subQ0])],"isStart":false})});}
            var Q4;
            {var subQ0=sQuery(id+"F0.wireOp",EDGE,"E25.7");var subQ1=sQuery(id+"F0.wireOp",EDGE,"E25.1");var subQ2=sQuery(id+"F0.wireOp",EDGE,"E25.6");var subQ3=sQuery(id+"F0.wireOp",EDGE,"E25.5");var subQ4=sQuery(id+"F0.wireOp",EDGE,"E25.4");var subQ5=sQuery(id+"F0.wireOp",EDGE,"E25.0");var subQ6=sQuery(id+"F0.wireOp",EDGE,"E25.2");var subQ7=sQuery(id+"F0.wireOp",EDGE,"E25.3");Q4=makeQuery(id+"F8.boolean.opBoolean","INTERSECT",EDGE,{"derivedFrom":[makeQuery(id+"F5.boolean.opBoolean","SPLIT",FACE,{"disambiguationData":[TD([makeQuery(id+"F2.opExtrude","SWEPT_FACE",FACE,{"disambiguationData":[OSD([subQ5])]})])],"derivedFrom":makeQuery(id+"F3.boolean.opBoolean","COPY",FACE,{"derivedFrom":makeQuery(id+"F3.opExtrude","CAP_FACE",FACE,{"disambiguationData":[OSD([subQ5,subQ1,subQ6,subQ7,subQ4,subQ3,subQ2,subQ0])],"isStart":false})})}),makeQuery(id+"F8.opExtrude","SWEPT_FACE",FACE,{"disambiguationData":[OSD([sQuery(id+"F7.wireOp",EDGE,"E67")])]})]});}
            var Q5;
            Q5=makeQuery(id+"F8.boolean.opBoolean","INTERSECT",EDGE,{"disambiguationData":[OD(0.0)],"derivedFrom":[makeQuery(id+"F5.opExtrude","SWEPT_FACE",FACE,{"disambiguationData":[OSD([sQuery(id+"F4.wireOp",EDGE,"E30")])]}),makeQuery(id+"F8.opExtrude","SWEPT_FACE",FACE,{"disambiguationData":[OSD([sQuery(id+"F7.wireOp",EDGE,"E67")])]})]});
            fillet(context, id + "F14", {"entities" : qUnion([Q0, Q1, Q2, Q3, Q4, Q5]), "radius" : 3 * mm, "tangentPropagation" : true, "allowEdgeOverflow" : false});
        }
        {
            var Q0;
            Q0=makeQuery(id+"F1.opExtrude","CAP_EDGE",EDGE,{"disambiguationData":[OSD([sQuery(id+"F0.wireOp",EDGE,"E1.bottom")])],"isStart":false});
            fillet(context, id + "F15", {"entities" : qUnion([Q0]), "radius" : 2 * mm, "tangentPropagation" : true, "allowEdgeOverflow" : false});
        }
        {
            var Q0;
            {var subQ0=sQuery(id+"F0.wireOp",EDGE,"E21.filletArc");var subQ1=sQuery(id+"F0.wireOp",EDGE,"E7");var subQ2=sQuery(id+"F0.wireOp",EDGE,"E6");var subQ3=sQuery(id+"F0.wireOp",EDGE,"E5");var subQ4=sQuery(id+"F0.wireOp",EDGE,"E4");var subQ5=sQuery(id+"F0.wireOp",EDGE,"E22.filletArc");var subQ6=sQuery(id+"F0.wireOp",EDGE,"E1.bottom");var subQ7=sQuery(id+"F0.wireOp",EDGE,"E1.right");var subQ8=sQuery(id+"F0.wireOp",EDGE,"E1.top");var subQ9=sQuery(id+"F0.wireOp",EDGE,"E1.left");var subQ10=sQuery(id+"F0.wireOp",EDGE,"E23.filletArc");var subQ11=sQuery(id+"F0.wireOp",EDGE,"E24.filletArc");Q0=makeQuery(id+"F2.boolean.opBoolean","SPLIT",FACE,{"disambiguationData":[TD([makeQuery(id+"F1.opExtrude","SWEPT_FACE",FACE,{"disambiguationData":[OSD([subQ6])]})])],"derivedFrom":makeQuery(id+"F1.opExtrude","CAP_FACE",FACE,{"disambiguationData":[OSD([subQ6,subQ8,subQ9,subQ7,subQ4,subQ3,subQ2,subQ1,subQ0,subQ5,subQ10,subQ11])],"isStart":true})});}
            var sketch = newSketch(context, id + "F16", { "sketchPlane" : qUnion([Q0])});
            skCircle(sketch, "E79", {"center": v(2.86, 121.5) * mm, "radius": 6 * mm});
            skLineSegment(sketch, "E80", {"start": v(-30.07, 90) * mm, "end": v(-12.07, 108) * mm});
            skLineSegment(sketch, "E81", {"start": v(17.78, 108) * mm, "end": v(35.78, 90) * mm});
            skLineSegment(sketch, "E82", {"start": v(-12.07, 108) * mm, "end": v(-12.07, 120) * mm});
            skLineSegment(sketch, "E83", {"start": v(17.78, 108) * mm, "end": v(17.78, 120) * mm});
            skArc(sketch, "E84", {"start": v(17.78, 120) * mm, "mid": v(2.86, 136.5) * mm, "end": v(-12.07, 120) * mm});
            skLineSegment(sketch, "E85", {"start": v(2.86, 121.5) * mm, "end": v(2.86, 90) * mm, "construction": true});
            skLineSegment(sketch, "E86", {"start": v(80, 0) * mm, "end": v(-80, 0) * mm});
            skCircle(sketch, "E87.MirrorC", {"center": v(2.86, -121.5) * mm, "radius": 6 * mm});
            skArc(sketch, "E88.MirrorCS", {"start": v(17.78, -120) * mm, "mid": v(2.86, -136.5) * mm, "end": v(-12.07, -120) * mm});
            skLineSegment(sketch, "E89.MirrorCS", {"start": v(-30.07, -90) * mm, "end": v(-12.07, -108) * mm});
            skLineSegment(sketch, "E90.MirrorCS", {"start": v(17.78, -108) * mm, "end": v(17.78, -120) * mm});
            skLineSegment(sketch, "E91.MirrorCS", {"start": v(17.78, -108) * mm, "end": v(35.78, -90) * mm});
            skLineSegment(sketch, "E92.MirrorCS", {"start": v(2.86, -121.5) * mm, "end": v(2.86, -90) * mm, "construction": true});
            skLineSegment(sketch, "E93.MirrorCS", {"start": v(-12.07, -108) * mm, "end": v(-12.07, -120) * mm});
            skSolve(sketch);
        }
        {
            var Q0;
            {var subQ1=sQuery(id+"F16.wireOp",EDGE,"E80");Q0=makeQuery(id+"F16.imprint","IMPRINT",FACE,{"disambiguationData":[TD([[makeQuery(id+"F16.imprint","IMPRINT",EDGE,{"derivedFrom":subQ1}),-1.0]])]});}
            var Q1;
            Q1=makeQuery(id+"F16.imprint","IMPRINT",FACE,{"disambiguationData":[TD([[makeQuery(id+"F16.imprint","IMPRINT",EDGE,{"derivedFrom":sQuery(id+"F16.wireOp",EDGE,"E88.MirrorCS")}),-1.0]])]});
            var Q2;
            Q2=makeQuery(id+"F16.imprint","IMPRINT",FACE,{"disambiguationData":[TD([[makeQuery(id+"F16.imprint","IMPRINT",EDGE,{"derivedFrom":makeQuery(id+"F1.opExtrude","CAP_EDGE",EDGE,{"disambiguationData":[OSD([sQuery(id+"F0.wireOp",EDGE,"E4")])],"isStart":true})}),-1.0]])]});
            var Q3;
            Q3=makeQuery(id+"F16.imprint","IMPRINT",FACE,{"disambiguationData":[TD([[makeQuery(id+"F16.imprint","IMPRINT",EDGE,{"derivedFrom":makeQuery(id+"F1.opExtrude","CAP_EDGE",EDGE,{"disambiguationData":[OSD([sQuery(id+"F0.wireOp",EDGE,"E6")])],"isStart":true})}),-1.0]])]});
            var Q4;
            Q4=makeQuery(id+"F2.opExtrude","CAP_FACE",FACE,{"disambiguationData":[OSD([sQuery(id+"F0.wireOp",EDGE,"E12"),sQuery(id+"F0.wireOp",EDGE,"E13"),sQuery(id+"F0.wireOp",EDGE,"E14"),sQuery(id+"F0.wireOp",EDGE,"E15"),sQuery(id+"F0.wireOp",EDGE,"E17.filletArc"),sQuery(id+"F0.wireOp",EDGE,"E18.filletArc"),sQuery(id+"F0.wireOp",EDGE,"E19.filletArc"),sQuery(id+"F0.wireOp",EDGE,"E20.filletArc"),sQuery(id+"F0.wireOp",EDGE,"E25.0"),sQuery(id+"F0.wireOp",EDGE,"E25.1"),sQuery(id+"F0.wireOp",EDGE,"E25.2"),sQuery(id+"F0.wireOp",EDGE,"E25.3"),sQuery(id+"F0.wireOp",EDGE,"E25.4"),sQuery(id+"F0.wireOp",EDGE,"E25.5"),sQuery(id+"F0.wireOp",EDGE,"E25.6"),sQuery(id+"F0.wireOp",EDGE,"E25.7")])],"isStart":false});
            extrude(context, id + "F17", {"entities" : qUnion([Q0, Q1, Q2, Q3]), "endBound" : BoundingType.UP_TO_SURFACE, "endBoundEntityFace" : qUnion([Q4]), "depth" : 25 * mm});
        }
    });
